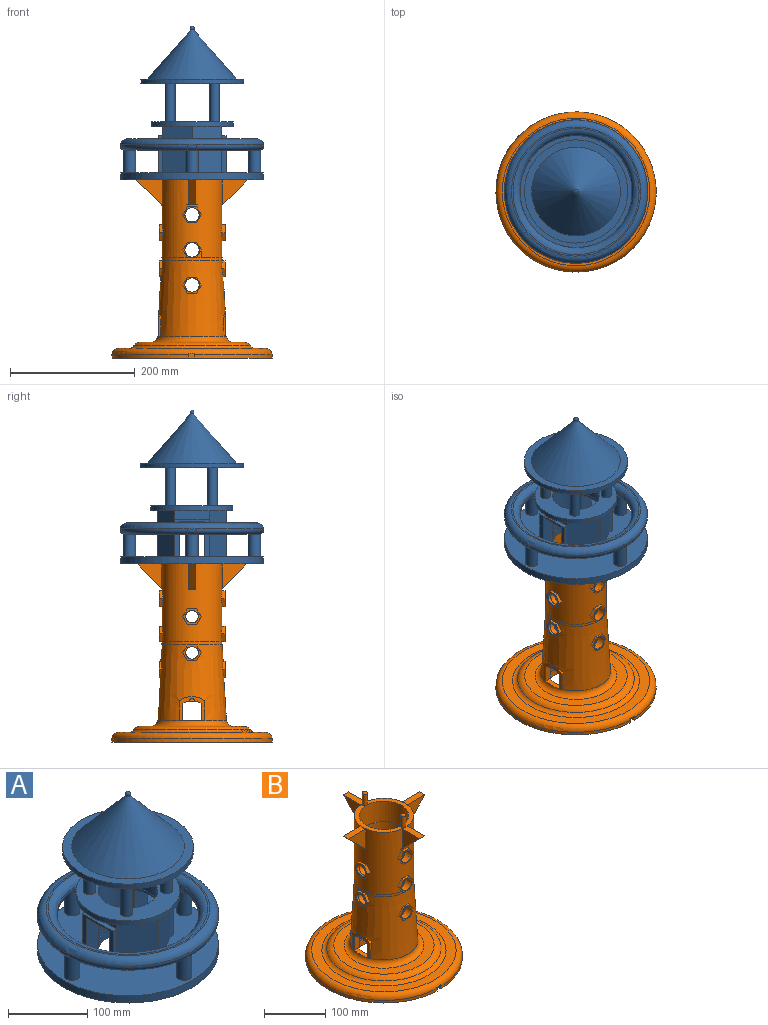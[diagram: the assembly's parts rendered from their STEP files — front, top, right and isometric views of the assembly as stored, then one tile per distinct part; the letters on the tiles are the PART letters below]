
ASSEMBLY  parts=2 mates=1
PART A: 93 faces, bbox 249.1x249.1x246.4 mm
  f0: plane 40.59x22.7mm, normal (0,0,-1), area 752.8mm2, adj f79,f80,f84,f92
  f1: plane 56.47x22.13mm, normal (0,-1,0), area 1249.6mm2, adj f6,f78,f91,f92
  f2: plane 56.47x22.41mm, normal (0,1,0), area 1265.4mm2, adj f6,f78,f91,f92
  f3: plane 59.68x0.52mm, normal (0,1,0), area 31.3mm2, adj f7,f66,f82,f92
  f4: plane 54.82x12.16mm, normal (0,0,1), area 22.2mm2, adj f66,f81,f83,f92
  f5: plane 59.68x0.52mm, normal (0,-1,0), area 31.3mm2, adj f65,f66,f82,f92
  f6: plane 228.6x228.6mm, normal (0,0,1), area 32754.8mm2, adj f1,f2,f17,f18,f19,f20,f21,f51
  f7: plane 52.92x10.69mm, normal (0,0,1), area 21mm2, adj f3,f66,f81,f92
  f8: plane 54.82x14.23mm, normal (-1,0,0), area 780.1mm2, adj f51,f52,f60,f89
  f9: plane 124.59x124.59mm, normal (0,0,1), area 7743.5mm2, adj f72,f75
  f10: plane 228.6x228.6mm, normal (0,0,-1), area 36452.1mm2, adj f17,f56,f58,f92
  f11: cylinder r=89.33mm len=9.52mm, axis (0,0,-1), area 16.1mm2, adj f25,f36
  f12: cylinder r=89.33mm len=9.43mm, axis (0,0,-1), area 15.4mm2, adj f25,f28
  f13: cylinder r=89.33mm len=9.52mm, axis (0,0,-1), area 16.1mm2, adj f25,f33
  f14: plane 100.1x100.02mm, normal (0,0,-1), area 1453.7mm2, adj f18,f21,f37,f49
  f15: plane 100.1x100.02mm, normal (0,0,-1), area 1453.7mm2, adj f18,f19,f29,f45
  f16: plane 100.1x100.02mm, normal (0,0,-1), area 1453.7mm2, adj f19,f20,f32,f44
  f17: cylinder r=114.3mm len=228.6mm, axis (0,0,-1), area 8026.2mm2, adj f6,f10
  f18: cylinder r=9.91mm len=36.32mm, axis (0,0,-1), area 2260.7mm2, adj f6,f14,f15,f31,f33,f35,f47
  f19: cylinder r=9.91mm len=36.32mm, axis (0,0,-1), area 2260.7mm2, adj f6,f15,f16,f27,f28,f30,f43
  f20: cylinder r=9.91mm len=36.32mm, axis (0,0,-1), area 2260.7mm2, adj f6,f16,f22,f34,f36,f38,f46
  f21: cylinder r=9.91mm len=36.32mm, axis (0,0,-1), area 2260.7mm2, adj f6,f14,f22,f39,f41,f42,f50
  f22: plane 100.1x100.02mm, normal (0,0,-1), area 1453.7mm2, adj f20,f21,f40,f48
  f23: cylinder r=89.33mm len=9.43mm, axis (0,0,-1), area 15.4mm2, adj f25,f41
  f24: plane 206.76x206.76mm, normal (0,0,1), area 1520.5mm2, adj f25,f26
  f25: torus R=101.01mm, axis (0,0,1), area 9288.7mm2, adj f11,f12,f13,f23,f24,f27,f29,f30
  f26: torus R=103.38mm, axis (0,0,1), area 10657.5mm2, adj f24,f43,f44,f45,f46,f47,f48,f49
  f27: bspline ~9.89x9.64mm, area 26.5mm2, adj f19,f25,f28,f29
  f28: bspline ~16.62x6.6mm, area 79.6mm2, adj f12,f19,f27,f30
  f29: torus R=97.08mm, axis (0,0,-1), area 1760.4mm2, adj f15,f25,f27,f31
  f30: bspline ~9.89x9.64mm, area 26.5mm2, adj f19,f25,f28,f32
  f31: bspline ~9.87x9.61mm, area 26.1mm2, adj f18,f25,f29,f33
  f32: torus R=97.08mm, axis (0,0,-1), area 1760.4mm2, adj f16,f25,f30,f34
  f33: bspline ~16.77x6.6mm, area 79.5mm2, adj f13,f18,f31,f35
  f34: bspline ~9.88x9.62mm, area 26.1mm2, adj f20,f25,f32,f36
  f35: bspline ~9.88x9.62mm, area 26.1mm2, adj f18,f25,f33,f37
  f36: bspline ~16.77x6.6mm, area 79.5mm2, adj f11,f20,f34,f38
  f37: torus R=97.08mm, axis (0,0,-1), area 1760.4mm2, adj f14,f25,f35,f39
  f38: bspline ~9.87x9.61mm, area 26.1mm2, adj f20,f25,f36,f40
  f39: bspline ~9.89x9.64mm, area 26.5mm2, adj f21,f25,f37,f41
  f40: torus R=97.08mm, axis (0,0,-1), area 1760.4mm2, adj f22,f25,f38,f42
  f41: bspline ~16.62x6.6mm, area 79.6mm2, adj f21,f23,f39,f42
  f42: bspline ~9.89x9.64mm, area 26.5mm2, adj f21,f25,f40,f41
  f43: bspline ~15.13x9.53mm, area 173.3mm2, adj f19,f26,f44,f45
  f44: torus R=107.32mm, axis (0,0,1), area 2251.4mm2, adj f16,f26,f43,f46
  f45: torus R=107.32mm, axis (0,0,1), area 2251.4mm2, adj f15,f26,f43,f47
  f46: bspline ~14.95x9.53mm, area 172.5mm2, adj f20,f26,f44,f48
  f47: bspline ~14.95x9.53mm, area 172.5mm2, adj f18,f26,f45,f49
  f48: torus R=107.32mm, axis (0,0,1), area 2251.4mm2, adj f22,f26,f46,f50
  f49: torus R=107.32mm, axis (0,0,1), area 2251.4mm2, adj f14,f26,f47,f50
  f50: bspline ~15.13x9.53mm, area 173.3mm2, adj f21,f26,f48,f49
  f51: plane 73.91x47.48mm, normal (-0.5,0.87,0), area 4052.3mm2, adj f6,f8,f55,f60,f90
  f52: plane 73.91x47.48mm, normal (-0.5,-0.87,0), area 4052.3mm2, adj f6,f8,f53,f60,f88
  f53: plane 73.91x47.48mm, normal (0.5,-0.87,0), area 4052.3mm2, adj f6,f52,f54,f60,f87
  f54: plane 54.82x14.23mm, normal (1,0,0), area 780.1mm2, adj f53,f55,f60,f86
  f55: plane 73.91x47.48mm, normal (0.5,0.87,0), area 4052.3mm2, adj f6,f51,f54,f60,f85
  f56: cylinder r=4.32mm len=27.43mm, axis (0,0,-1), area 744.3mm2, adj f10,f57
  f57: plane 8.64x8.64mm, normal (0,0,-1), area 58.6mm2, adj f56
  f58: cylinder r=4.32mm len=27.43mm, axis (0,0,-1), area 744.3mm2, adj f10,f59
  f59: plane 8.64x8.64mm, normal (0,0,-1), area 58.6mm2, adj f58
  f60: plane 131.43x131.43mm, normal (0,0,-1), area 5758.3mm2, adj f8,f51,f52,f53,f54,f55,f61
  f61: cylinder r=65.72mm len=131.43mm, axis (0,0,-1), area 3146.3mm2, adj f60,f63
  f62: cylinder r=37.66mm len=75.33mm, axis (0,0,-1), area 1803.2mm2, adj f63,f64
  f63: plane 131.43x131.43mm, normal (0,0,1), area 8335.1mm2, adj f61,f62,f67,f68,f69,f70
  f64: plane 76.2x76.2mm, normal (0,0,-1), area 104.1mm2, adj f62,f66
  f65: plane 52.92x10.69mm, normal (0,0,1), area 21mm2, adj f5,f66,f83,f92
  f66: cylinder r=38.1mm len=76.2mm, axis (0,0,-1), area 10389.8mm2, adj f3,f4,f5,f7,f64,f65,f81,f82
  f67: cylinder r=7.84mm len=61.21mm, axis (0,0,-1), area 3015.8mm2, adj f63,f71
  f68: cylinder r=7.87mm len=61.21mm, axis (0,0,-1), area 3028.5mm2, adj f63,f71
  f69: cylinder r=7.84mm len=61.21mm, axis (0,0,-1), area 3015.8mm2, adj f63,f71
  f70: cylinder r=7.87mm len=61.21mm, axis (0,0,-1), area 3028.5mm2, adj f63,f71
  f71: plane 165.37x165.37mm, normal (0,0,-1), area 16253.5mm2, adj f67,f68,f69,f70,f72,f73
  f72: cylinder r=37.63mm len=75.26mm, axis (0,0,-1), area 1801.5mm2, adj f9,f71
  f73: cylinder r=82.68mm len=165.37mm, axis (0,0,-1), area 3958.7mm2, adj f71,f74
  f74: plane 165.37x165.37mm, normal (0,0,1), area 5573.9mm2, adj f73,f76
  f75: cone r=0mm half-angle=41.5deg, axis (0,0,-1), area 18384mm2, adj f9
  f76: cone r=0mm half-angle=41.1deg, axis (0,0,-1), area 24146.6mm2, adj f74,f77
  f77: sphere r=3.53mm, area 136.5mm2, adj f76
  f78: plane 40.59x22.41mm, normal (0,0,-1), area 740.9mm2, adj f1,f2,f91,f92
  f79: plane 56.47x22.42mm, normal (0,-1,0), area 1266.1mm2, adj f0,f6,f84,f92
  f80: plane 56.47x22.7mm, normal (0,1,0), area 1281.9mm2, adj f0,f6,f84,f92
  f81: plane 59.68x0.52mm, normal (0,1,0), area 31.3mm2, adj f4,f7,f66,f92
  f82: plane 54.82x12.16mm, normal (0,0,1), area 22.2mm2, adj f3,f5,f66,f92
  f83: plane 59.68x0.52mm, normal (0,-1,0), area 31.3mm2, adj f4,f65,f66,f92
  f84: plane 59.68x54.82mm, normal (1,0,0), area 980mm2, adj f0,f6,f79,f80,f85,f86,f87
  f85: plane 59.68x6.9mm, normal (0,1,0), area 411.6mm2, adj f6,f55,f84,f86
  f86: plane 54.82x6.9mm, normal (0,0,1), area 378.1mm2, adj f54,f84,f85,f87
  f87: plane 59.68x6.9mm, normal (0,-1,0), area 411.6mm2, adj f6,f53,f84,f86
  f88: plane 59.68x6.6mm, normal (0,-1,0), area 394.2mm2, adj f6,f52,f89,f91
  f89: plane 54.82x6.6mm, normal (0,0,1), area 362.1mm2, adj f8,f88,f90,f91
  f90: plane 59.68x6.6mm, normal (0,1,0), area 394.2mm2, adj f6,f51,f89,f91
  f91: plane 59.68x54.82mm, normal (-1,0,0), area 980mm2, adj f1,f2,f6,f78,f88,f89,f90
  f92: cylinder r=37.74mm len=75.48mm, axis (0,0,1), area 5134.6mm2, adj f0,f1,f2,f3,f4,f5,f6,f7
PART B: 209 faces, bbox 278.4x278.4x313.5 mm
  f0: cylinder r=128.27mm len=256.54mm, axis (0,0,1), area 4049mm2, adj f1,f2,f206,f207
  f1: plane 256.54x256.49mm, normal (0,0,-1), area 43122.4mm2, adj f0,f70,f206,f207
  f2: torus R=118.11mm, axis (0,0,-1), area 12466.9mm2, adj f0,f69,f206,f207,f208
  f3: cone r=39.88mm half-angle=3.1deg, axis (0,0,-1), area 18318.6mm2, adj f19,f20,f21,f22,f23,f24,f28,f29
  f4: plane 25.81x1.58mm, normal (0,1,0), area 20.3mm2, adj f11,f12,f205
  f5: plane 25.81x1.58mm, normal (0,-1,0), area 20.3mm2, adj f7,f12,f205
  f6: plane 5.37x3.78mm, normal (0,0,-1), area 8.2mm2, adj f12,f190,f193,f205
  f7: plane 5.37x3.78mm, normal (0,0,-1), area 8.2mm2, adj f5,f8,f12,f205
  f8: plane 25.8x1.5mm, normal (0,1,0), area 19.2mm2, adj f7,f12,f205
  f9: plane 27.5x10.6mm, normal (0,-1,0), area 290.7mm2, adj f10,f14,f181,f201,f202,f205
  f10: plane 12.93x5.51mm, normal (0,0,-1), area 13.9mm2, adj f9,f12,f15,f17,f188,f189,f202,f205
  f11: plane 12.93x5.51mm, normal (0,0,-1), area 13.9mm2, adj f4,f12,f15,f16,f195,f196,f203,f205
  f12: cone r=39.88mm half-angle=3.1deg, axis (0,0,-1), area 8013.3mm2, adj f4,f5,f6,f7,f8,f10,f11,f16
  f13: cone r=48.51mm half-angle=3.1deg, axis (0,0,-1), area 34435.1mm2, adj f15,f38,f109,f110,f111,f112,f113,f114
  f14: cone r=48.51mm half-angle=3.1deg, axis (0,0,-1), area 39.9mm2, adj f9,f15,f181,f182,f186,f194,f201,f202
  f15: torus R=65.4mm, axis (0,0,-1), area 5681.4mm2, adj f10,f11,f13,f14,f16,f17,f18,f68
  f16: plane 9.05x0.12mm, normal (0,-1,0), area 1.1mm2, adj f11,f12,f15,f178
  f17: plane 9.05x0.12mm, normal (0,-1,0), area 1.1mm2, adj f10,f12,f15,f183
  f18: cone r=48.51mm half-angle=3.1deg, axis (0,0,-1), area 39.9mm2, adj f15,f179,f180,f185,f187,f195,f200,f203
  f19: plane 12.91x7.54mm, normal (0.87,0,-0.5), area 39.8mm2, adj f3,f20,f24,f177
  f20: plane 14.66x3.64mm, normal (0,0,-1), area 43.7mm2, adj f3,f19,f124,f177
  f21: plane 12.91x7.54mm, normal (-0.87,0,-0.5), area 39.8mm2, adj f3,f22,f123,f176
  f22: plane 12.88x7.51mm, normal (-0.87,0,0.5), area 29.4mm2, adj f3,f21,f126,f176
  f23: plane 14.66x2.25mm, normal (0,0,1), area 23.2mm2, adj f3,f24,f125,f177
  f24: plane 12.88x7.51mm, normal (0.87,0,0.5), area 29.4mm2, adj f3,f19,f23,f177
  f25: cylinder r=11.43mm len=22.86mm, axis (0,-1,0), area 930.3mm2, adj f115,f177
  f26: cylinder r=11.43mm len=22.86mm, axis (0,-1,0), area 930.3mm2, adj f37,f101
  f27: cylinder r=11.43mm len=22.86mm, axis (0,-1,0), area 930.3mm2, adj f37,f93
  f28: plane 14.66x0.83mm, normal (0,0,1), area 2.2mm2, adj f3,f33,f166,f175
  f29: plane 12.88x7.51mm, normal (0,0.87,0.5), area 7.7mm2, adj f3,f30,f165,f174
  f30: plane 12.93x7.56mm, normal (0,0.87,-0.5), area 18.1mm2, adj f3,f29,f31,f174
  f31: plane 14.66x2.22mm, normal (0,0,-1), area 22.7mm2, adj f3,f30,f169,f174
  f32: plane 12.93x7.56mm, normal (0,-0.87,-0.5), area 18.1mm2, adj f3,f33,f168,f175
  f33: plane 12.88x7.51mm, normal (0,-0.87,0.5), area 7.7mm2, adj f3,f28,f32,f175
  f34: cylinder r=10.16mm len=20.32mm, axis (-1,0,0), area 54.9mm2, adj f172,f175
  f35: cylinder r=48.51mm len=124.92mm, axis (0,0,1), area 32733.2mm2, adj f36,f38,f39,f42,f43,f44,f46,f47
  f36: cylinder r=48.51mm len=12.69mm, axis (0,0,1), area 47.7mm2, adj f35,f38,f95
  f37: cylinder r=39.88mm len=86.11mm, axis (0,0,1), area 19263mm2, adj f3,f26,f27,f57,f129,f130,f147,f148
  f38: torus R=124.71mm, axis (0,0,1), area 1266.9mm2, adj f13,f35,f36,f95,f96,f97,f104,f105
  f39: plane 97.03x97.03mm, normal (0,0,1), area 2183.4mm2, adj f35,f58,f73,f76
  f40: plane 100.11x100.11mm, normal (0,0,-1), area 821.3mm2, adj f67,f70
  f41: plane 94.74x94.74mm, normal (0,0,-1), area 67.2mm2, adj f12,f67
  f42: plane 39.94x11.94mm, normal (0,0,1), area 473.6mm2, adj f35,f43,f44,f63
  f43: plane 39.94x39.44mm, normal (1,0,0), area 787.6mm2, adj f35,f42,f63
  f44: plane 39.9x39.4mm, normal (-1,0,0), area 786.1mm2, adj f35,f42,f63
  f45: plane 11.83x0.35mm, normal (-1,0,0), area 4.2mm2, adj f47,f48,f49,f60
  f46: plane 11.83x0.65mm, normal (0,0,-1), area 4.3mm2, adj f35,f47,f48,f60
  f47: plane 40.79x39.89mm, normal (0,-1,0), area 833.4mm2, adj f35,f45,f46,f49,f60
  f48: plane 40.71x39.89mm, normal (0,1,0), area 830.5mm2, adj f35,f45,f46,f49,f60
  f49: plane 40.79x11.83mm, normal (0,0,1), area 479mm2, adj f35,f45,f47,f48
  f50: plane 40.56x39.89mm, normal (0,-1,0), area 834.2mm2, adj f35,f52,f53,f59
  f51: plane 40.49x39.89mm, normal (0,1,0), area 831.3mm2, adj f35,f52,f53,f59
  f52: plane 11.83x1.26mm, normal (0,0,-1), area 11.7mm2, adj f35,f50,f51,f59
  f53: plane 40.56x11.83mm, normal (0,0,1), area 476.3mm2, adj f35,f50,f51,f59
  f54: plane 39.9x39.4mm, normal (-1,0,0), area 786.1mm2, adj f35,f55,f65
  f55: plane 39.94x11.94mm, normal (0,0,1), area 473.6mm2, adj f35,f54,f56,f65
  f56: plane 39.94x39.44mm, normal (1,0,0), area 787.6mm2, adj f35,f55,f65
  f57: plane 80.64x80.64mm, normal (0,0,1), area 111mm2, adj f37,f58
  f58: cylinder r=40.32mm len=80.64mm, axis (0,0,1), area 10359.6mm2, adj f39,f57
  f59: plane 39.89x39.3mm, normal (0.71,0,-0.7), area 662.2mm2, adj f50,f51,f52,f53
  f60: plane 40.14x39.54mm, normal (-0.7,0,-0.71), area 666.3mm2, adj f45,f46,f47,f48
  f61: plane 12.42x1.05mm, normal (-0.7,0,-0.71), area 3.9mm2, adj f35,f62
  f62: plane 11.72x0.36mm, normal (0,0,1), area 2.8mm2, adj f35,f61
  f63: plane 40.54x40.04mm, normal (0,-0.7,-0.71), area 682mm2, adj f35,f42,f43,f44,f64
  f64: plane 18.85x0.92mm, normal (0,0,1), area 11.6mm2, adj f35,f63
  f65: plane 40.54x40.04mm, normal (0,0.7,-0.71), area 682mm2, adj f35,f54,f55,f56,f66
  f66: plane 18.85x0.92mm, normal (0,0,1), area 11.6mm2, adj f35,f65
  f67: cylinder r=47.37mm len=94.74mm, axis (0,0,1), area 2948.4mm2, adj f40,f41
  f68: plane 164.21x164.21mm, normal (0,0,1), area 7740.6mm2, adj f15,f72
  f69: plane 236.22x236.22mm, normal (0,0,1), area 11397.9mm2, adj f2,f71
  f70: cylinder r=50.05mm len=100.11mm, axis (0,0,1), area 4722.9mm2, adj f1,f40,f206,f207,f208
  f71: torus R=101.6mm, axis (0,0,-1), area 5832.8mm2, adj f69,f72
  f72: torus R=82.1mm, axis (0,0,1), area 7280.6mm2, adj f68,f71
  f73: cylinder r=4.06mm len=21.84mm, axis (0,0,-1), area 557.8mm2, adj f39,f79
  f74: plane 1.02x1.02mm, normal (0,0,1), area 0.8mm2, adj f79
  f75: plane 0.72x0.02mm, normal (0,0,-1), area 0mm2, adj f35,f76
  f76: cylinder r=4.06mm len=21.84mm, axis (0,0,-1), area 557.8mm2, adj f39,f75,f78
  f77: plane 1.02x1.02mm, normal (0,0,1), area 0.8mm2, adj f78
  f78: torus R=0.51mm, axis (0,0,1), area 97.3mm2, adj f76,f77
  f79: torus R=0.51mm, axis (0,0,1), area 97.3mm2, adj f73,f74
  f80: plane 29.33x25.4mm, normal (0,-1,0), area 148.3mm2, adj f81,f82,f83,f84,f85,f86,f130
  f81: plane 12.82x7.45mm, normal (-0.87,0,0.5), area 82.6mm2, adj f35,f80,f82,f86
  f82: plane 14.66x4.88mm, normal (0,0,1), area 66mm2, adj f35,f80,f81,f83
  f83: plane 12.82x7.45mm, normal (0.87,0,0.5), area 82.6mm2, adj f35,f80,f82,f84
  f84: plane 12.82x7.45mm, normal (0.87,0,-0.5), area 82.6mm2, adj f35,f80,f83,f85
  f85: plane 14.66x4.88mm, normal (0,0,-1), area 66mm2, adj f35,f80,f84,f86
  f86: plane 12.82x7.45mm, normal (-0.87,0,-0.5), area 82.6mm2, adj f35,f80,f81,f85
  f87: plane 12.82x7.45mm, normal (-0.87,0,-0.5), area 82.6mm2, adj f35,f88,f89,f93
  f88: plane 12.82x7.45mm, normal (-0.87,0,0.5), area 82.6mm2, adj f35,f87,f92,f93
  f89: plane 14.66x4.88mm, normal (0,0,-1), area 66mm2, adj f35,f87,f90,f93
  f90: plane 12.82x7.45mm, normal (0.87,0,-0.5), area 82.6mm2, adj f35,f89,f91,f93
  f91: plane 12.82x7.45mm, normal (0.87,0,0.5), area 82.6mm2, adj f35,f90,f92,f93
  f92: plane 14.66x4.88mm, normal (0,0,1), area 66mm2, adj f35,f88,f91,f93
  f93: plane 29.33x25.4mm, normal (0,1,0), area 148.3mm2, adj f27,f87,f88,f89,f90,f91,f92
  f94: plane 29.33x25.4mm, normal (0,-1,0), area 148.3mm2, adj f95,f96,f97,f98,f99,f100,f129
  f95: plane 12.82x7.45mm, normal (0.87,0,-0.5), area 82.6mm2, adj f36,f38,f94,f96,f100
  f96: plane 14.66x4.88mm, normal (0,0,-1), area 66mm2, adj f38,f94,f95,f97
  f97: plane 12.82x7.45mm, normal (-0.87,0,-0.5), area 82.6mm2, adj f35,f38,f94,f96,f98
  f98: plane 12.82x7.45mm, normal (-0.87,0,0.5), area 82.6mm2, adj f35,f94,f97,f99
  f99: plane 14.66x4.88mm, normal (0,0,1), area 66mm2, adj f35,f94,f98,f100
  f100: plane 12.82x7.45mm, normal (0.87,0,0.5), area 82.6mm2, adj f35,f94,f95,f99
  f101: plane 29.33x25.4mm, normal (0,1,0), area 148.3mm2, adj f26,f102,f103,f104,f105,f106,f107
  f102: plane 14.66x4.88mm, normal (0,0,1), area 66mm2, adj f35,f101,f103,f107
  f103: plane 12.82x7.45mm, normal (0.87,0,0.5), area 82.6mm2, adj f35,f101,f102,f106
  f104: plane 14.66x4.88mm, normal (0,0,-1), area 66mm2, adj f38,f101,f105,f106
  f105: plane 12.82x7.45mm, normal (-0.87,0,-0.5), area 82.6mm2, adj f35,f38,f101,f104,f107
  f106: plane 12.82x7.45mm, normal (0.87,0,-0.5), area 82.6mm2, adj f35,f38,f101,f103,f104
  f107: plane 12.82x7.45mm, normal (-0.87,0,0.5), area 82.6mm2, adj f35,f101,f102,f105
  f108: plane 29.33x25.4mm, normal (0,-1,0), area 148.3mm2, adj f109,f110,f111,f112,f113,f114,f128
  f109: plane 12.85x7.48mm, normal (0.87,0,-0.5), area 43.3mm2, adj f13,f108,f110,f114
  f110: plane 14.66x1.88mm, normal (0,0,-1), area 22.5mm2, adj f13,f108,f109,f111
  f111: plane 12.85x7.48mm, normal (-0.87,0,-0.5), area 43.3mm2, adj f13,f108,f110,f112
  f112: plane 12.77x7.4mm, normal (-0.87,0,0.5), area 53.6mm2, adj f13,f108,f111,f113
  f113: plane 14.66x3.28mm, normal (0,0,1), area 42.9mm2, adj f13,f108,f112,f114
  f114: plane 12.77x7.4mm, normal (0.87,0,0.5), area 53.6mm2, adj f13,f108,f109,f113
  f115: plane 29.33x25.4mm, normal (0,1,0), area 148.3mm2, adj f25,f116,f117,f118,f119,f120,f121
  f116: plane 14.66x1.88mm, normal (0,0,-1), area 22.5mm2, adj f13,f115,f117,f120
  f117: plane 12.85x7.48mm, normal (-0.87,0,-0.5), area 43.3mm2, adj f13,f115,f116,f118
  f118: plane 12.77x7.4mm, normal (-0.87,0,0.5), area 53.6mm2, adj f13,f115,f117,f119
  f119: plane 14.66x3.28mm, normal (0,0,1), area 42.9mm2, adj f13,f115,f118,f121
  f120: plane 12.85x7.48mm, normal (0.87,0,-0.5), area 43.3mm2, adj f13,f115,f116,f121
  f121: plane 12.77x7.4mm, normal (0.87,0,0.5), area 53.6mm2, adj f13,f115,f119,f120
  f122: plane 12.91x7.54mm, normal (0.87,0,-0.5), area 39.8mm2, adj f3,f123,f127,f176
  f123: plane 14.66x3.64mm, normal (0,0,-1), area 43.7mm2, adj f3,f21,f122,f176
  f124: plane 12.91x7.54mm, normal (-0.87,0,-0.5), area 39.8mm2, adj f3,f20,f125,f177
  f125: plane 12.88x7.51mm, normal (-0.87,0,0.5), area 29.4mm2, adj f3,f23,f124,f177
  f126: plane 14.66x2.25mm, normal (0,0,1), area 23.2mm2, adj f3,f22,f127,f176
  f127: plane 12.88x7.51mm, normal (0.87,0,0.5), area 29.4mm2, adj f3,f122,f126,f176
  f128: cylinder r=11.43mm len=22.86mm, axis (0,-1,0), area 930.3mm2, adj f108,f176
  f129: cylinder r=11.43mm len=22.86mm, axis (0,-1,0), area 930.3mm2, adj f37,f94
  f130: cylinder r=11.43mm len=22.86mm, axis (0,-1,0), area 930.3mm2, adj f37,f80
  f131: cylinder r=10.16mm len=20.32mm, axis (-1,0,0), area 275.6mm2, adj f132,f147
  f132: plane 29.33x25.4mm, normal (1,0,0), area 234.4mm2, adj f131,f133,f134,f135,f136,f137,f138
  f133: plane 14.66x4.88mm, normal (0,0,-1), area 66mm2, adj f35,f132,f134,f138
  f134: plane 12.82x7.45mm, normal (0,-0.87,-0.5), area 82.6mm2, adj f35,f132,f133,f135
  f135: plane 12.82x7.45mm, normal (0,-0.87,0.5), area 82.6mm2, adj f35,f132,f134,f136
  f136: plane 14.66x4.88mm, normal (0,0,1), area 66mm2, adj f35,f132,f135,f137
  f137: plane 12.82x7.45mm, normal (0,0.87,0.5), area 82.6mm2, adj f35,f132,f136,f138
  f138: plane 12.82x7.45mm, normal (0,0.87,-0.5), area 82.6mm2, adj f35,f132,f133,f137
  f139: plane 29.33x25.4mm, normal (-1,0,0), area 234.4mm2, adj f140,f141,f142,f143,f144,f145,f146
  f140: plane 12.82x7.45mm, normal (0,0.87,0.5), area 82.6mm2, adj f35,f139,f141,f145
  f141: plane 12.82x7.45mm, normal (0,0.87,-0.5), area 82.6mm2, adj f35,f139,f140,f142
  f142: plane 14.66x4.88mm, normal (0,0,-1), area 66mm2, adj f35,f139,f141,f143
  f143: plane 12.82x7.45mm, normal (0,-0.87,-0.5), area 82.6mm2, adj f35,f139,f142,f144
  f144: plane 12.82x7.45mm, normal (0,-0.87,0.5), area 82.6mm2, adj f35,f139,f143,f145
  f145: plane 14.66x4.88mm, normal (0,0,1), area 66mm2, adj f35,f139,f140,f144
  f146: cylinder r=10.16mm len=20.32mm, axis (-1,0,0), area 275.6mm2, adj f139,f148
  f147: cylinder r=10.16mm len=20.32mm, axis (1,0,0), area 551.3mm2, adj f37,f131
  f148: cylinder r=10.16mm len=20.32mm, axis (1,0,0), area 551.3mm2, adj f37,f146
  f149: cylinder r=10.16mm len=20.32mm, axis (-1,0,0), area 254.9mm2, adj f150,f171
  f150: plane 29.33x25.4mm, normal (-1,0,0), area 234.4mm2, adj f149,f151,f152,f153,f154,f155,f156
  f151: plane 14.66x4.72mm, normal (0,0,1), area 63.8mm2, adj f13,f150,f152,f156
  f152: plane 12.77x7.4mm, normal (0,0.87,0.5), area 75mm2, adj f13,f150,f151,f153
  f153: plane 12.86x7.49mm, normal (0,0.87,-0.5), area 64.7mm2, adj f13,f150,f152,f154
  f154: plane 14.66x3.32mm, normal (0,0,-1), area 43.4mm2, adj f13,f150,f153,f155
  f155: plane 12.86x7.49mm, normal (0,-0.87,-0.5), area 64.7mm2, adj f13,f150,f154,f156
  f156: plane 12.77x7.4mm, normal (0,-0.87,0.5), area 75mm2, adj f13,f150,f151,f155
  f157: plane 29.33x25.4mm, normal (1,0,0), area 234.4mm2, adj f158,f159,f160,f161,f162,f163,f164
  f158: plane 12.86x7.49mm, normal (0,0.87,-0.5), area 64.7mm2, adj f13,f157,f159,f162
  f159: plane 14.66x3.32mm, normal (0,0,-1), area 43.4mm2, adj f13,f157,f158,f163
  f160: plane 12.77x7.4mm, normal (0,-0.87,0.5), area 75mm2, adj f13,f157,f161,f163
  f161: plane 14.66x4.72mm, normal (0,0,1), area 63.8mm2, adj f13,f157,f160,f162
  f162: plane 12.77x7.4mm, normal (0,0.87,0.5), area 75mm2, adj f13,f157,f158,f161
  f163: plane 12.86x7.49mm, normal (0,-0.87,-0.5), area 64.7mm2, adj f13,f157,f159,f160
  f164: cylinder r=10.16mm len=20.32mm, axis (-1,0,0), area 253.9mm2, adj f157,f172
  f165: plane 14.66x0.83mm, normal (0,0,1), area 2.2mm2, adj f3,f29,f170,f174
  f166: plane 12.88x7.51mm, normal (0,0.87,0.5), area 7.7mm2, adj f3,f28,f167,f175
  f167: plane 12.93x7.56mm, normal (0,0.87,-0.5), area 18.1mm2, adj f3,f166,f168,f175
  f168: plane 14.66x2.22mm, normal (0,0,-1), area 22.7mm2, adj f3,f32,f167,f175
  f169: plane 12.93x7.56mm, normal (0,-0.87,-0.5), area 18.1mm2, adj f3,f31,f170,f174
  f170: plane 12.88x7.51mm, normal (0,-0.87,0.5), area 7.7mm2, adj f3,f165,f169,f174
  f171: cylinder r=10.16mm len=20.32mm, axis (1,0,0), area 558.3mm2, adj f149,f173
  f172: cylinder r=10.16mm len=20.32mm, axis (1,0,0), area 558.1mm2, adj f34,f164
  f173: cylinder r=10.16mm len=20.32mm, axis (-1,0,0), area 54.9mm2, adj f171,f174
  f174: cylinder r=39.88mm len=29.33mm, axis (0,0,1), area 241.8mm2, adj f29,f30,f31,f165,f169,f170,f173
  f175: cylinder r=39.88mm len=29.33mm, axis (0,0,1), area 241.8mm2, adj f28,f32,f33,f34,f166,f167,f168
  f176: cylinder r=39.88mm len=29.33mm, axis (0,0,1), area 154mm2, adj f21,f22,f122,f123,f126,f127,f128
  f177: cylinder r=39.88mm len=29.33mm, axis (0,0,1), area 154mm2, adj f19,f20,f23,f24,f25,f124,f125
  f178: plane 29.67x11.07mm, normal (0,0,1), area 260.4mm2, adj f12,f15,f16,f179
  f179: plane 27.52x10.54mm, normal (0,1,0), area 248.7mm2, adj f12,f15,f18,f178,f180,f205
  f180: cylinder r=31.26mm len=29.64mm, axis (1,0,0), area 276.7mm2, adj f18,f179,f195,f205
  f181: cylinder r=31.26mm len=29.64mm, axis (1,0,0), area 238.2mm2, adj f9,f14,f182,f205
  f182: plane 27.52x10.54mm, normal (0,1,0), area 248.7mm2, adj f12,f14,f15,f181,f183,f205
  f183: plane 29.67x11.07mm, normal (0,0,1), area 260.4mm2, adj f12,f15,f17,f182
  f184: cylinder r=34.59mm len=40.73mm, axis (1,0,0), area 62.7mm2, adj f13,f196,f198,f203
  f185: cylinder r=31.19mm len=9.62mm, axis (1,0,0), area 8.4mm2, adj f18,f195,f203
  f186: cylinder r=31.19mm len=9.9mm, axis (1,0,0), area 9mm2, adj f14,f194,f202
  f187: cylinder r=31.19mm len=9.9mm, axis (1,0,0), area 9mm2, adj f18,f200,f203
  f188: plane 25.81x1.58mm, normal (0,1,0), area 20.3mm2, adj f10,f12,f205
  f189: plane 31.8x3.81mm, normal (0,1,0), area 91.1mm2, adj f10,f13,f15,f197,f202
  f190: plane 25.81x1.58mm, normal (0,-1,0), area 20.3mm2, adj f6,f12,f205
  f191: plane 31.8x3.86mm, normal (0,-1,0), area 92.5mm2, adj f13,f15,f192,f197,f202
  f192: plane 5.37x1.97mm, normal (0,0,-1), area 5.4mm2, adj f15,f191,f194,f202
  f193: plane 25.8x1.5mm, normal (0,1,0), area 19.2mm2, adj f6,f12,f205
  f194: plane 27.51x1.72mm, normal (0,1,0), area 25.7mm2, adj f14,f15,f186,f192,f202
  f195: plane 27.5x10.6mm, normal (0,-1,0), area 290.7mm2, adj f11,f18,f180,f185,f203,f205
  f196: plane 31.8x3.81mm, normal (0,1,0), area 91.1mm2, adj f11,f13,f15,f184,f203
  f197: cylinder r=34.59mm len=40.73mm, axis (1,0,0), area 86.8mm2, adj f13,f189,f191,f202
  f198: plane 31.8x3.86mm, normal (0,-1,0), area 92.5mm2, adj f13,f15,f184,f199,f203
  f199: plane 5.37x1.97mm, normal (0,0,-1), area 5.4mm2, adj f15,f198,f200,f203
  f200: plane 27.51x1.72mm, normal (0,1,0), area 25.7mm2, adj f15,f18,f187,f199,f203
  f201: cylinder r=31.19mm len=9.62mm, axis (1,0,0), area 8.4mm2, adj f9,f14,f202
  f202: plane 40.73x38.42mm, normal (-1,0,0), area 552.1mm2, adj f9,f10,f14,f186,f189,f191,f192,f194
  f203: plane 40.73x38.42mm, normal (1,0,0), area 552.1mm2, adj f11,f18,f184,f185,f187,f195,f196,f198
  f204: plane 90.46x90.46mm, normal (0,0,-1), area 309.1mm2, adj f3,f205
  f205: cylinder r=45.23mm len=90.46mm, axis (0,0,-1), area 6096.3mm2, adj f4,f5,f6,f7,f8,f9,f10,f11
  f206: plane 78.3x7.89mm, normal (-1,0,0), area 616.1mm2, adj f0,f1,f2,f70,f208
  f207: plane 78.4x7.88mm, normal (1,0,0), area 616.9mm2, adj f0,f1,f2,f70,f208
  f208: plane 78.11x8.89mm, normal (0,0,-1), area 692.2mm2, adj f2,f70,f206,f207
PLACE A t=(-124.01,-92.66,159.92)mm
PLACE B t=(-124.01,-92.74,47.68)mm
MATE fastened A.f58 <-> B.f76  axis (0,0,-1) through (-124.01,-137.21,159.92)mm
